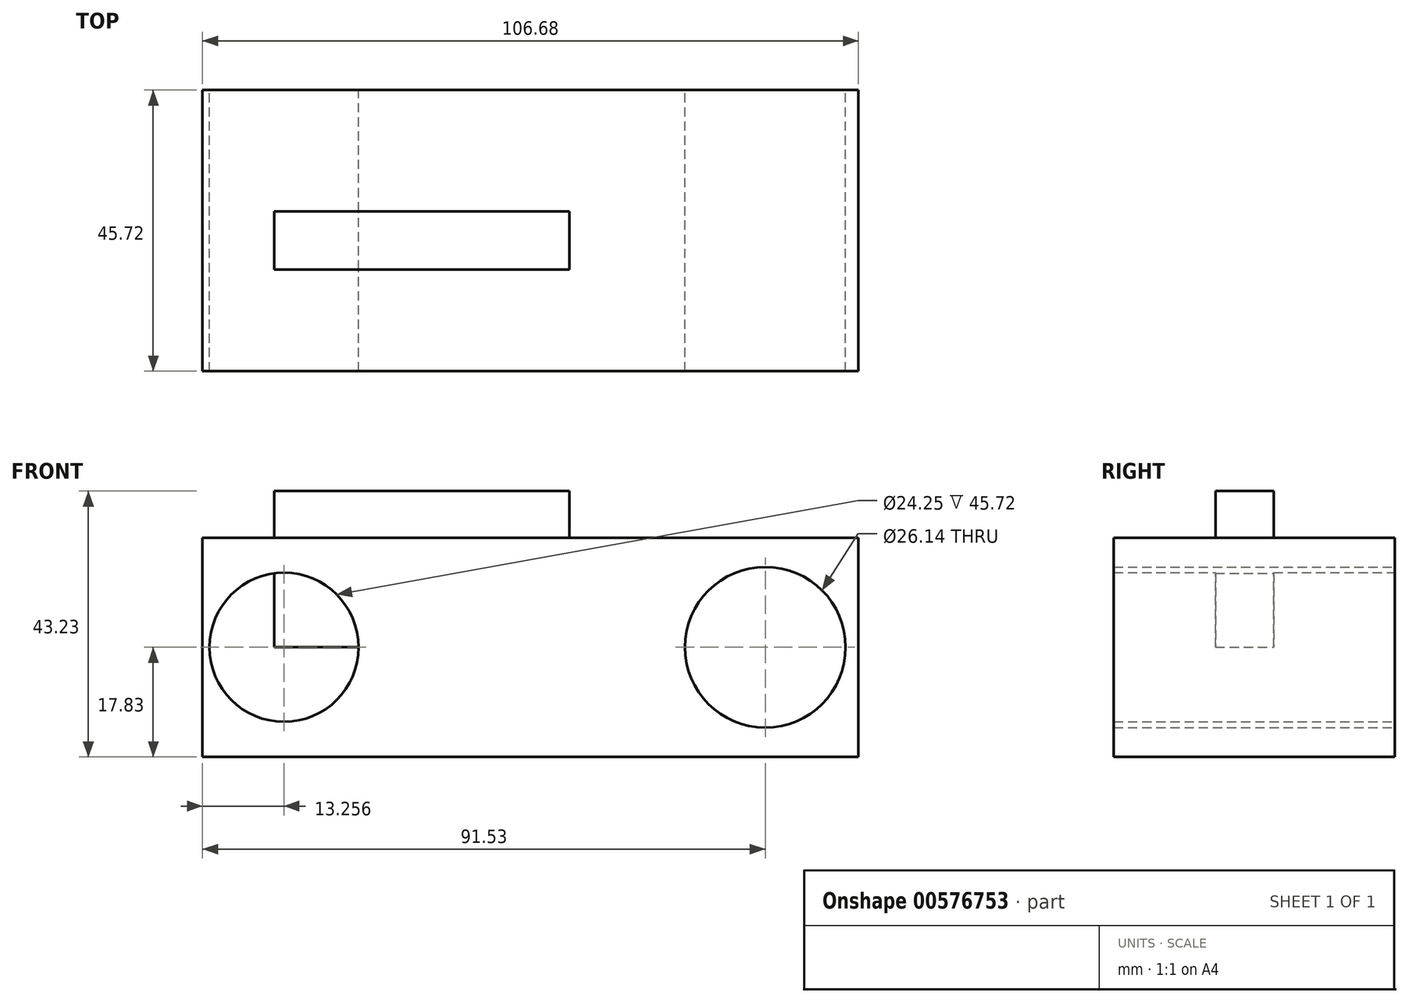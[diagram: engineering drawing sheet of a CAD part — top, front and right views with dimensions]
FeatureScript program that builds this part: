
annotation { "Feature Type Name" : "Feature", "Feature Type Description" : "" }
export const myFeature = defineFeature(function(context is Context, id is Id, definition is map)
    precondition{}
    {
        {
            var Q0;
            Q0=qCreatedBy(makeId("Front.planeOp"),FACE);
            var sketch = newSketch(context, id + "F0", { "sketchPlane" : qUnion([Q0])});
            skLineSegment(sketch, "E0.bottom", {"start": v(53.34, -17.83) * mm, "end": v(-53.34, -17.83) * mm});
            skLineSegment(sketch, "E0.top", {"start": v(53.34, 17.83) * mm, "end": v(-53.34, 17.83) * mm});
            skLineSegment(sketch, "E0.left", {"start": v(53.34, -17.83) * mm, "end": v(53.34, 17.83) * mm});
            skLineSegment(sketch, "E0.right", {"start": v(-53.34, -17.83) * mm, "end": v(-53.34, 17.83) * mm});
            skPoint(sketch, "E0.middle", {"position": v(0, 0) * mm});
            skCircle(sketch, "E1", {"center": v(-40.08, 0) * mm, "radius": 12.13 * mm});
            skCircle(sketch, "E2", {"center": v(38.2, 0) * mm, "radius": 13.07 * mm});
            skSolve(sketch);
        }
        {
            var Q0;
            Q0=makeQuery(id+"F0.imprint","IMPRINT",FACE,{"disambiguationData":[TD([[makeQuery(id+"F0.imprint","IMPRINT",EDGE,{"derivedFrom":sQuery(id+"F0.wireOp",EDGE,"E0.bottom")}),-1.0]])]});
            extrude(context, id + "F1", {"entities" : qUnion([Q0]), "depth" : 45.72 * mm, "offsetDistance" : 25.4 * mm});
        }
        {
            var Q0;
            Q0=qCreatedBy(makeId("Top.planeOp"),FACE);
            var sketch = newSketch(context, id + "F2", { "sketchPlane" : qUnion([Q0])});
            skLineSegment(sketch, "E3.bottom", {"start": v(6.31, -29.2) * mm, "end": v(-41.66, -29.2) * mm});
            skLineSegment(sketch, "E3.top", {"start": v(6.31, -19.73) * mm, "end": v(-41.66, -19.73) * mm});
            skLineSegment(sketch, "E3.left", {"start": v(6.31, -29.2) * mm, "end": v(6.31, -19.73) * mm});
            skLineSegment(sketch, "E3.right", {"start": v(-41.66, -29.2) * mm, "end": v(-41.66, -19.73) * mm});
            skPoint(sketch, "E3.middle", {"position": v(-17.67, -24.46) * mm});
            skSolve(sketch);
        }
        {
            var Q0;
            Q0 = qSketchRegion(id + "F2", true);
            extrude(context, id + "F3", {"entities" : qUnion([Q0]), "operationType" : NewBodyOperationType.ADD, "depth" : 25.4 * mm, "offsetDistance" : 25.4 * mm});
        }
    });
